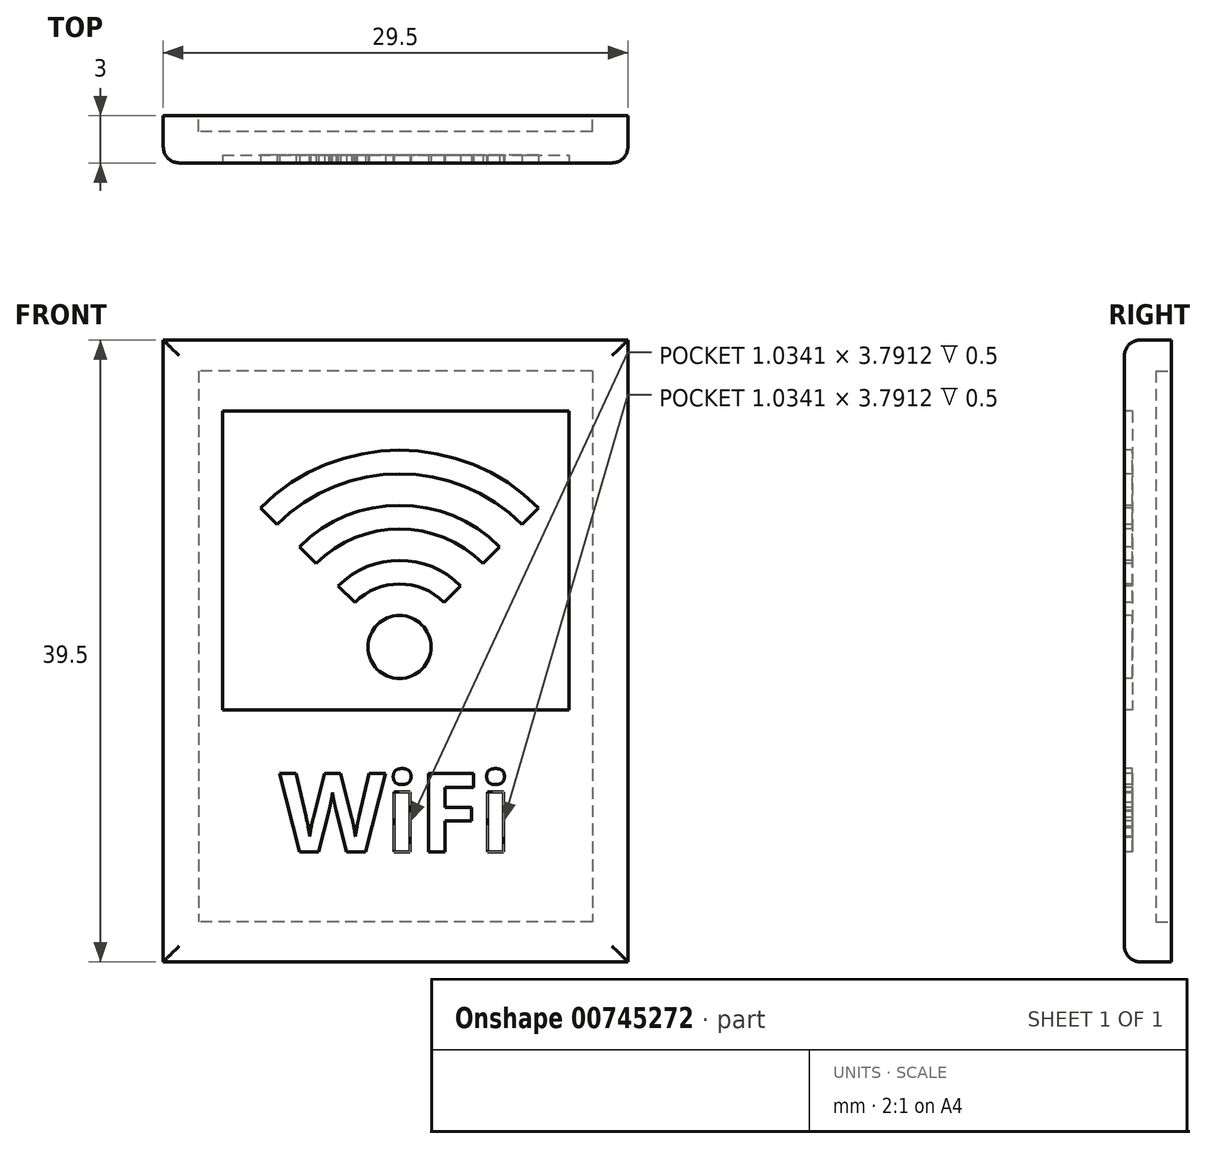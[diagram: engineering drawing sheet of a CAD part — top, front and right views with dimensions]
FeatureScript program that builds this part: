
annotation { "Feature Type Name" : "Feature", "Feature Type Description" : "" }
export const myFeature = defineFeature(function(context is Context, id is Id, definition is map)
    precondition{}
    {
        {
            var Q0;
            Q0=qCreatedBy(makeId("Front.planeOp"),FACE);
            var sketch = newSketch(context, id + "F0", { "sketchPlane" : qUnion([Q0])});
            skLineSegment(sketch, "E0.bottom", {"start": v(0, 0) * mm, "end": v(29.5, 0) * mm});
            skLineSegment(sketch, "E0.top", {"start": v(0, 39.5) * mm, "end": v(29.5, 39.5) * mm});
            skLineSegment(sketch, "E0.left", {"start": v(0, 0) * mm, "end": v(0, 39.5) * mm});
            skLineSegment(sketch, "E0.right", {"start": v(29.5, 0) * mm, "end": v(29.5, 39.5) * mm});
            skSolve(sketch);
        }
        {
            var Q0;
            Q0 = qSketchRegion(id + "F0", true);
            extrude(context, id + "F1", {"entities" : qUnion([Q0]), "depth" : 3 * mm, "offsetDistance" : 25 * mm});
        }
        {
            var Q0;
            Q0=makeQuery(id+"F1.opExtrude","CAP_EDGE",EDGE,{"disambiguationData":[OSD([sQuery(id+"F0.wireOp",EDGE,"E0.right")])],"isStart":false});
            var Q1;
            Q1=makeQuery(id+"F1.opExtrude","CAP_EDGE",EDGE,{"disambiguationData":[OSD([sQuery(id+"F0.wireOp",EDGE,"E0.bottom")])],"isStart":false});
            var Q2;
            Q2=makeQuery(id+"F1.opExtrude","CAP_EDGE",EDGE,{"disambiguationData":[OSD([sQuery(id+"F0.wireOp",EDGE,"E0.left")])],"isStart":false});
            var Q3;
            Q3=makeQuery(id+"F1.opExtrude","CAP_EDGE",EDGE,{"disambiguationData":[OSD([sQuery(id+"F0.wireOp",EDGE,"E0.top")])],"isStart":false});
            fillet(context, id + "F2", {"entities" : qUnion([Q0, Q1, Q2, Q3]), "radius" : 1 * mm, "tangentPropagation" : true, "allowEdgeOverflow" : false});
        }
        {
            var Q0;
            Q0=makeQuery(id+"F1.opExtrude","CAP_FACE",FACE,{"disambiguationData":[OSD([sQuery(id+"F0.wireOp",EDGE,"E0.bottom"),sQuery(id+"F0.wireOp",EDGE,"E0.top"),sQuery(id+"F0.wireOp",EDGE,"E0.left"),sQuery(id+"F0.wireOp",EDGE,"E0.right")])],"isStart":false});
            var sketch = newSketch(context, id + "F3", { "sketchPlane" : qUnion([Q0])});
            skCircle(sketch, "E1", {"center": v(15, 20) * mm, "radius": 2 * mm});
            skArc(sketch, "E2", {"start": v(9.7, 25.3) * mm, "mid": v(15, 27.5) * mm, "end": v(20.3, 25.3) * mm});
            skArc(sketch, "E3", {"start": v(8.64, 26.36) * mm, "mid": v(15, 29) * mm, "end": v(21.36, 26.36) * mm});
            skLineSegment(sketch, "E4", {"start": v(20.3, 25.3) * mm, "end": v(21.36, 26.36) * mm});
            skLineSegment(sketch, "E5", {"start": v(9.7, 25.3) * mm, "end": v(8.64, 26.36) * mm});
            skArc(sketch, "E6", {"start": v(7.22, 27.78) * mm, "mid": v(15, 31) * mm, "end": v(22.78, 27.78) * mm});
            skArc(sketch, "E7", {"start": v(6.16, 28.84) * mm, "mid": v(15, 32.5) * mm, "end": v(23.84, 28.84) * mm});
            skLineSegment(sketch, "E8", {"start": v(22.78, 27.78) * mm, "end": v(23.84, 28.84) * mm});
            skLineSegment(sketch, "E9", {"start": v(7.22, 27.78) * mm, "end": v(6.16, 28.84) * mm});
            skArc(sketch, "E10", {"start": v(12.17, 22.83) * mm, "mid": v(15, 24) * mm, "end": v(17.83, 22.83) * mm});
            skArc(sketch, "E11", {"start": v(11.11, 23.89) * mm, "mid": v(15, 25.5) * mm, "end": v(18.89, 23.89) * mm});
            skLineSegment(sketch, "E12", {"start": v(17.83, 22.83) * mm, "end": v(18.89, 23.89) * mm});
            skLineSegment(sketch, "E13", {"start": v(12.17, 22.83) * mm, "end": v(11.11, 23.89) * mm});
            skLineSegment(sketch, "E14.bottom", {"start": v(3.75, 35) * mm, "end": v(25.75, 35) * mm});
            skLineSegment(sketch, "E14.top", {"start": v(3.75, 16) * mm, "end": v(25.75, 16) * mm});
            skLineSegment(sketch, "E14.left", {"start": v(3.75, 35) * mm, "end": v(3.75, 16) * mm});
            skLineSegment(sketch, "E14.right", {"start": v(25.75, 35) * mm, "end": v(25.75, 16) * mm});
            skSolve(sketch);
        }
        {
            var Q0;
            Q0=makeQuery(id+"F3.imprint","IMPRINT",FACE,{"disambiguationData":[TD([[makeQuery(id+"F3.imprint","IMPRINT",EDGE,{"derivedFrom":sQuery(id+"F3.wireOp",EDGE,"E1")}),-1.0]])]});
            extrude(context, id + "F4", {"entities" : qUnion([Q0]), "operationType" : NewBodyOperationType.REMOVE, "oppositeDirection" : true, "depth" : 0.5 * mm, "offsetDistance" : 25 * mm});
        }
        {
            var Q0;
            {var subQ0=sQuery(id+"F0.wireOp",EDGE,"E0.right");var subQ1=sQuery(id+"F0.wireOp",EDGE,"E0.left");var subQ2=sQuery(id+"F0.wireOp",EDGE,"E0.top");var subQ3=sQuery(id+"F0.wireOp",EDGE,"E0.bottom");Q0=makeQuery(id+"F4.boolean.opBoolean","SPLIT",FACE,{"disambiguationData":[TD([makeQuery(id+"F2.opFillet","BLEND_FACE",FACE,{"disambiguationData":[OSD([subQ3])]})])],"derivedFrom":makeQuery(id+"F1.opExtrude","CAP_FACE",FACE,{"disambiguationData":[OSD([subQ3,subQ2,subQ1,subQ0])],"isStart":false})});}
            var sketch = newSketch(context, id + "F5", { "sketchPlane" : qUnion([Q0])});
            skText(sketch, "E15", { "text": "WiFi", "fontName": "OpenSans-Bold.ttf"});
            const initialGuessF5  = {"E15": [0.00739, 0.007, 1, 0, 0.005]};
            skSetInitialGuess(sketch, initialGuessF5);
            skSolve(sketch);
        }
        {
            var Q0;
            Q0 = qSketchRegion(id + "F5", true);
            extrude(context, id + "F6", {"entities" : qUnion([Q0]), "operationType" : NewBodyOperationType.REMOVE, "oppositeDirection" : true, "depth" : 0.5 * mm, "offsetDistance" : 25 * mm});
        }
        {
            var Q0;
            Q0=makeQuery(id+"F1.opExtrude","CAP_FACE",FACE,{"disambiguationData":[OSD([sQuery(id+"F0.wireOp",EDGE,"E0.bottom"),sQuery(id+"F0.wireOp",EDGE,"E0.top"),sQuery(id+"F0.wireOp",EDGE,"E0.left"),sQuery(id+"F0.wireOp",EDGE,"E0.right")])],"isStart":true});
            var sketch = newSketch(context, id + "F7", { "sketchPlane" : qUnion([Q0])});
            skLineSegment(sketch, "E16.bottom", {"start": v(-27.25, 37.54) * mm, "end": v(-2.25, 37.54) * mm});
            skLineSegment(sketch, "E16.top", {"start": v(-27.25, 2.54) * mm, "end": v(-2.25, 2.54) * mm});
            skLineSegment(sketch, "E16.left", {"start": v(-27.25, 37.54) * mm, "end": v(-27.25, 2.54) * mm});
            skLineSegment(sketch, "E16.right", {"start": v(-2.25, 37.54) * mm, "end": v(-2.25, 2.54) * mm});
            skSolve(sketch);
        }
        {
            var Q0;
            Q0 = qSketchRegion(id + "F7", true);
            extrude(context, id + "F8", {"entities" : qUnion([Q0]), "operationType" : NewBodyOperationType.REMOVE, "oppositeDirection" : true, "depth" : 1 * mm, "offsetDistance" : 25 * mm});
        }
    });
